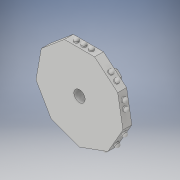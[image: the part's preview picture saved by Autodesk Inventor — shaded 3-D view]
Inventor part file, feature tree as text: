
AUTODESK INVENTOR PART (.ipt)
format: ipt  version: 2017 (Build 210142000, 142)  size: 301,568 bytes
history: native  units: in
note: dims shown in document units (in); Inventor stores cm internally (conversion verified against a paired STEP export)
features: extrude x5, sketch x5, pattern_circular x2, fillet x2
ambient origin geometry x8: Origin, YZ Plane, XZ Plane, XY Plane, X Axis, Y Axis, Z Axis, Center Point
bodies: Solid1 (feature_tree)
feature tree (14):
  extrude  "Extrusion1"  Depth=0.1181in TaperAngle=0.0deg
  extrude  "Extrusion2"  Depth=0.15in TaperAngle=0.0deg
  pattern_circular  "Circular Pattern1"  Count=8 Angle=360.0deg
  extrude  "Extrusion3"  TaperAngle=0.0deg  [1 undecoded]
  fillet  "Fillet1"  Radius=0.201in
  extrude  "Extrusion4"  Depth=0.0315in
  pattern_circular  "Circular Pattern2"  [2 undecoded]
  extrude  "Extrusion5"  Depth=0.0315in TaperAngle=360.0deg
  fillet  "Fillet2"  [1 undecoded]
  sketch  "Sketch1"  dims[d0=1.141in d1=0.1181in d2=0.0in]
  sketch  "Sketch2"  dims[d4=12.5984in d5=0.6in d6=360.0deg d7=0.04in d8=0.04in d9=0.075in d10=0.15in d11=0.0in d12=3.1496in d13=360.0deg]
  sketch  "Sketch3"  dims[d15=0.063in d16=0.1in d17=0.1in d18=0.063in d19=0.063in d20=0.0575in d21=0.059in d22=0.0in d23=0.059in d24=0.059in d25=0.236in d27=0.0in d28=0.201in]
  sketch  "Sketch4"  dims[d29=0.0472in d30=0.0in d31=0.0315in]
  sketch  "Sketch5"  dims[d32=0.15in d33=0.0472in d34=0.0in d35=3.5433in d36=360.0deg d38=0.0in d39=0.0in d40=0.0315in]
note: 4 required parameter values undecoded (feature->parameter linkage not recoverable at this tier; creation-order binding heuristic only, values carry confidence <= 0.55)
